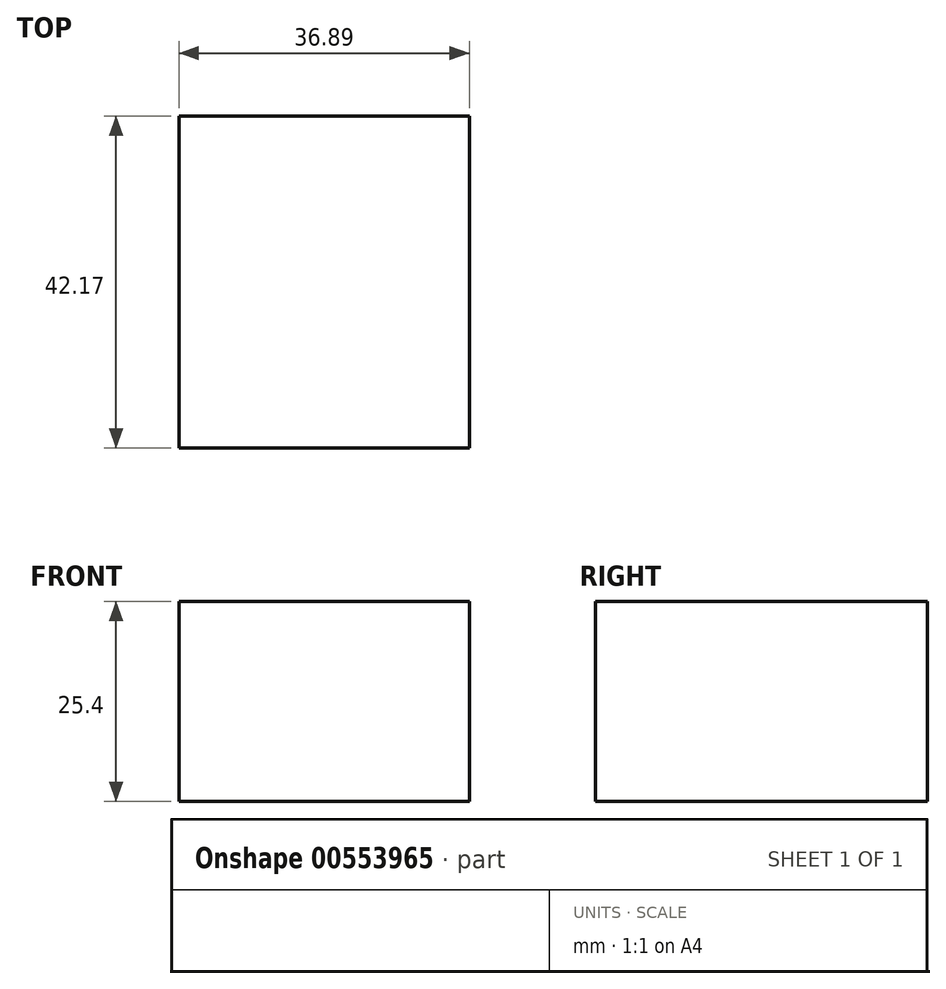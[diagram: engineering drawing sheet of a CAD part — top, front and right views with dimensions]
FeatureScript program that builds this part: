
annotation { "Feature Type Name" : "Feature", "Feature Type Description" : "" }
export const myFeature = defineFeature(function(context is Context, id is Id, definition is map)
    precondition{}
    {
        {
            var Q0;
            Q0=qCreatedBy(makeId("Top.planeOp"),FACE);
            var sketch = newSketch(context, id + "F0", { "sketchPlane" : qUnion([Q0])});
            skLineSegment(sketch, "E0.bottom", {"start": v(0, 0) * mm, "end": v(36.89, 0) * mm});
            skLineSegment(sketch, "E0.top", {"start": v(0, 42.17) * mm, "end": v(36.89, 42.17) * mm});
            skLineSegment(sketch, "E0.left", {"start": v(0, 0) * mm, "end": v(0, 42.17) * mm});
            skLineSegment(sketch, "E0.right", {"start": v(36.89, 0) * mm, "end": v(36.89, 42.17) * mm});
            skSolve(sketch);
        }
        {
            var Q0;
            Q0 = qSketchRegion(id + "F0", true);
            extrude(context, id + "F1", {"entities" : qUnion([Q0]), "depth" : 25.4 * mm, "offsetDistance" : 25.4 * mm});
        }
    });
